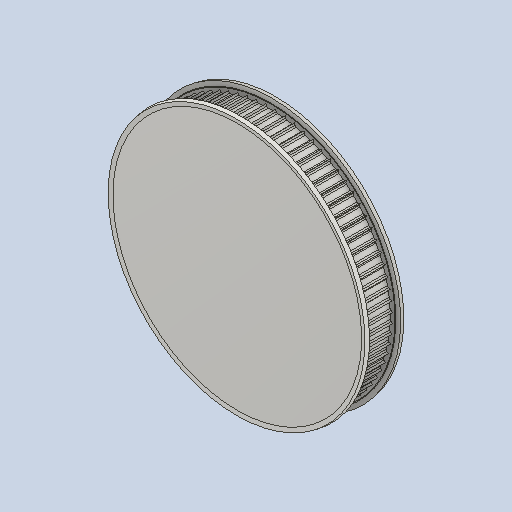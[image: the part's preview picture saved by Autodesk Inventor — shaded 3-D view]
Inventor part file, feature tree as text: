
AUTODESK INVENTOR PART (.ipt)
format: ipt  version: 2024 (Build 280153000, 153)  size: 570,368 bytes
history: native  units: mm (DEFAULTED — no unit token found)
features: other x3, extrude x2, fillet x1, pattern_circular x1
ambient origin geometry x8: Origin, YZ Plane, XZ Plane, XY Plane, X Axis, Y Axis, Z Axis, Center Point
bodies: Solid1 (feature_tree)
feature tree (7):
  other  "Pulley Sketch"
  extrude  "Base Body"  Depth=63.661977mm
  extrude  "Tooth"  Depth=0.3mm
  fillet  "Tooth Fillet"  Radius=1.25mm
  pattern_circular  "Teeth"  [2 undecoded]
  other  "Left flange"
  other  "Right flange"
note: 2 required parameter values undecoded (feature->parameter linkage not recoverable at this tier; creation-order binding heuristic only, values carry confidence <= 0.55)
